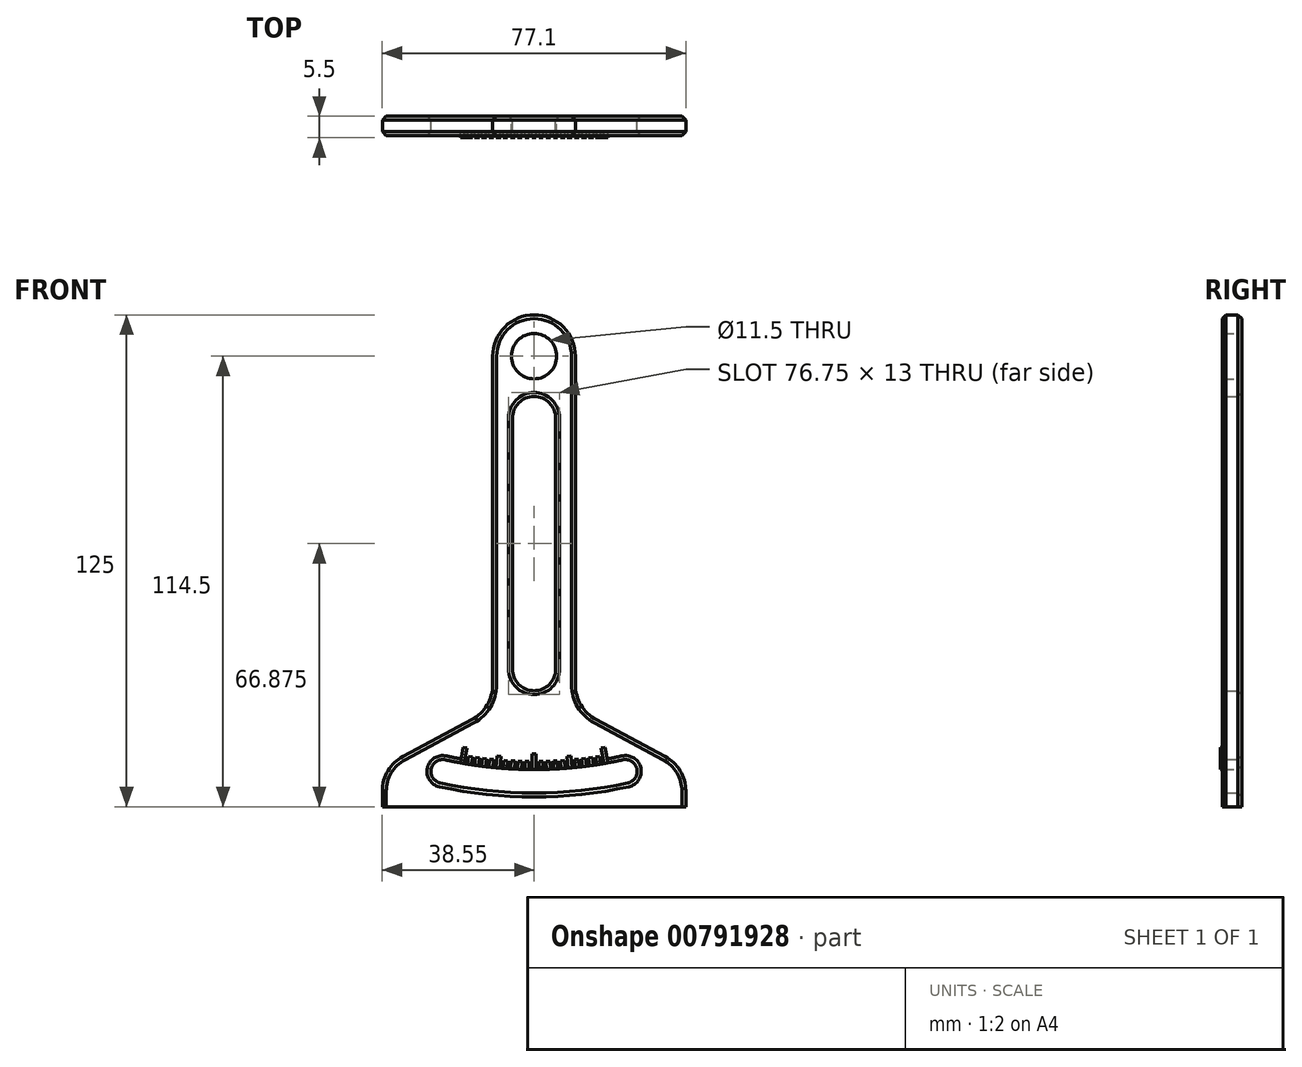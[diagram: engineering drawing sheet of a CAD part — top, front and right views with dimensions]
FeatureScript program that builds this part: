
annotation { "Feature Type Name" : "Feature", "Feature Type Description" : "" }
export const myFeature = defineFeature(function(context is Context, id is Id, definition is map)
    precondition{}
    {
        {
            var Q0;
            Q0=qCreatedBy(makeId("Front.planeOp"),FACE);
            var sketch = newSketch(context, id + "F0", { "sketchPlane" : qUnion([Q0])});
            skLineSegment(sketch, "E0", {"start": v(0, 62.5) * mm, "end": v(0, -62.5) * mm, "construction": true});
            skPoint(sketch, "E1", {"position": v(0, 0) * mm});
            skLineSegment(sketch, "E2", {"start": v(0, 62.5) * mm, "end": v(0, 57.5) * mm, "construction": true});
            skLineSegment(sketch, "E3", {"start": v(0, 57.5) * mm, "end": v(0, 52) * mm, "construction": true});
            skCircle(sketch, "E4", {"center": v(0, 52) * mm, "radius": 5.75 * mm});
            skLineSegment(sketch, "E5", {"start": v(-28.55, -62.5) * mm, "end": v(28.55, -62.5) * mm});
            skPoint(sketch, "E6", {"position": v(0, -62.5) * mm});
            skLineSegment(sketch, "E7", {"start": v(0, 52) * mm, "end": v(28.55, -62.5) * mm, "construction": true});
            skLineSegment(sketch, "E8", {"start": v(28.55, -62.5) * mm, "end": v(38.55, -62.5) * mm});
            skLineSegment(sketch, "E9", {"start": v(38.55, -62.5) * mm, "end": v(38.55, -52.5) * mm});
            skLineSegment(sketch, "E10", {"start": v(0, -62.5) * mm, "end": v(0, -37.5) * mm, "construction": true});
            skLineSegment(sketch, "E11", {"start": v(-10.5, -37.5) * mm, "end": v(10.5, -37.5) * mm, "construction": true});
            skPoint(sketch, "E12", {"position": v(0, -37.5) * mm});
            skLineSegment(sketch, "E13", {"start": v(38.55, -52.5) * mm, "end": v(10.5, -37.5) * mm});
            skLineSegment(sketch, "E14", {"start": v(10.5, -37.5) * mm, "end": v(10.5, 52) * mm});
            skLineSegment(sketch, "E15", {"start": v(28.55, -62.5) * mm, "end": v(26.13, -52.8) * mm, "construction": true});
            skLineSegment(sketch, "E16.MirrorCS", {"start": v(-38.55, -52.5) * mm, "end": v(-10.5, -37.5) * mm});
            skLineSegment(sketch, "E17.MirrorCS", {"start": v(-10.5, -37.5) * mm, "end": v(-10.5, 52) * mm});
            skLineSegment(sketch, "E18.MirrorCS", {"start": v(-38.55, -62.5) * mm, "end": v(-38.55, -52.5) * mm});
            skLineSegment(sketch, "E19.MirrorCS", {"start": v(-28.55, -62.5) * mm, "end": v(-38.55, -62.5) * mm});
            skLineSegment(sketch, "E20.MirrorCS", {"start": v(0, 52) * mm, "end": v(-28.55, -62.5) * mm, "construction": true});
            skLineSegment(sketch, "E21.MirrorCS", {"start": v(-28.55, -62.5) * mm, "end": v(-26.13, -52.8) * mm, "construction": true});
            skArc(sketch, "E22", {"start": v(-26.13, -52.8) * mm, "mid": v(0, -56) * mm, "end": v(26.13, -52.8) * mm, "construction": true});
            skArc(sketch, "E23.0", {"start": v(-25.4, -49.89) * mm, "mid": v(0, -53) * mm, "end": v(25.4, -49.89) * mm});
            skArc(sketch, "E24.0", {"start": v(-26.85, -55.7) * mm, "mid": v(0, -59) * mm, "end": v(26.85, -55.7) * mm});
            skLineSegment(sketch, "E25", {"start": v(-26.85, -55.7) * mm, "end": v(-25.4, -49.89) * mm});
            skLineSegment(sketch, "E26", {"start": v(26.85, -55.7) * mm, "end": v(25.4, -49.89) * mm});
            skArc(sketch, "E27", {"start": v(10.5, 52) * mm, "mid": v(0, 62.5) * mm, "end": v(-10.5, 52) * mm});
            skLineSegment(sketch, "E28", {"start": v(0, 46.25) * mm, "end": v(0, 36.25) * mm, "construction": true});
            skLineSegment(sketch, "E29", {"start": v(0, -37.5) * mm, "end": v(0, -27.5) * mm, "construction": true});
            skArc(sketch, "E30", {"start": v(-5.5, -27.5) * mm, "mid": v(0, -33) * mm, "end": v(5.5, -27.5) * mm});
            skArc(sketch, "E31", {"start": v(5.5, 36.25) * mm, "mid": v(0, 41.75) * mm, "end": v(-5.5, 36.25) * mm});
            skLineSegment(sketch, "E32", {"start": v(-5.5, 36.25) * mm, "end": v(-5.5, -27.5) * mm});
            skLineSegment(sketch, "E33", {"start": v(5.5, 36.25) * mm, "end": v(5.5, -27.5) * mm});
            skSolve(sketch);
        }
        {
            var Q0;
            Q0=makeQuery(id+"F0.imprint","IMPRINT",FACE,{"disambiguationData":[TD([[makeQuery(id+"F0.imprint","IMPRINT",EDGE,{"derivedFrom":sQuery(id+"F0.wireOp",EDGE,"E4")}),-1.0]])]});
            extrude(context, id + "F1", {"entities" : qUnion([Q0]), "depth" : 5 * mm, "offsetDistance" : 25 * mm});
        }
        {
            var Q0;
            Q0=makeQuery(id+"F1.opExtrude","CAP_FACE",FACE,{"disambiguationData":[OSD([sQuery(id+"F0.wireOp",EDGE,"E4"),sQuery(id+"F0.wireOp",EDGE,"E5"),sQuery(id+"F0.wireOp",EDGE,"E8"),sQuery(id+"F0.wireOp",EDGE,"E9"),sQuery(id+"F0.wireOp",EDGE,"E13"),sQuery(id+"F0.wireOp",EDGE,"E14"),sQuery(id+"F0.wireOp",EDGE,"E16.MirrorCS"),sQuery(id+"F0.wireOp",EDGE,"E17.MirrorCS"),sQuery(id+"F0.wireOp",EDGE,"E18.MirrorCS"),sQuery(id+"F0.wireOp",EDGE,"E19.MirrorCS"),sQuery(id+"F0.wireOp",EDGE,"E23.0"),sQuery(id+"F0.wireOp",EDGE,"E24.0"),sQuery(id+"F0.wireOp",EDGE,"E25"),sQuery(id+"F0.wireOp",EDGE,"E26"),sQuery(id+"F0.wireOp",EDGE,"E27")])],"isStart":false});
            var sketch = newSketch(context, id + "F2", { "sketchPlane" : qUnion([Q0])});
            skLineSegment(sketch, "E34", {"start": v(1.8, -50.99) * mm, "end": v(2, -62.5) * mm, "construction": true});
            skLineSegment(sketch, "E35", {"start": v(0, 52) * mm, "end": v(0, -62.5) * mm, "construction": true});
            skLineSegment(sketch, "E36", {"start": v(1.83, -52.99) * mm, "end": v(1.8, -50.99) * mm, "construction": true});
            skLineSegment(sketch, "E37", {"start": v(1.3, -51) * mm, "end": v(2.3, -50.98) * mm});
            skPoint(sketch, "E38", {"position": v(1.8, -50.99) * mm});
            skLineSegment(sketch, "E39", {"start": v(1.3, -51) * mm, "end": v(1.33, -53) * mm});
            skLineSegment(sketch, "E40", {"start": v(2.3, -50.98) * mm, "end": v(2.33, -52.99) * mm});
            skLineSegment(sketch, "E41", {"start": v(2.33, -52.99) * mm, "end": v(1.33, -53) * mm});
            skLineSegment(sketch, "E42", {"start": v(0, -53) * mm, "end": v(0, -49) * mm, "construction": true});
            skLineSegment(sketch, "E43", {"start": v(-0.5, -49) * mm, "end": v(0.5, -49) * mm});
            skPoint(sketch, "E44", {"position": v(0, -49) * mm});
            skLineSegment(sketch, "E45", {"start": v(-0.5, -49) * mm, "end": v(-0.5, -53) * mm});
            skLineSegment(sketch, "E46", {"start": v(-0.5, -53) * mm, "end": v(0.5, -53) * mm});
            skLineSegment(sketch, "E47", {"start": v(0.5, -53) * mm, "end": v(0.5, -49) * mm});
            skLineSegment(sketch, "E48", {"start": v(3.6, -50.94) * mm, "end": v(4, -62.5) * mm, "construction": true});
            skLineSegment(sketch, "E49", {"start": v(5.4, -50.86) * mm, "end": v(6, -62.5) * mm, "construction": true});
            skLineSegment(sketch, "E50", {"start": v(7.19, -50.75) * mm, "end": v(8, -62.5) * mm, "construction": true});
            skLineSegment(sketch, "E51", {"start": v(8.9, -49.62) * mm, "end": v(10.02, -62.5) * mm, "construction": true});
            skLineSegment(sketch, "E52", {"start": v(10.77, -50.44) * mm, "end": v(12.03, -62.5) * mm, "construction": true});
            skLineSegment(sketch, "E53", {"start": v(12.55, -50.24) * mm, "end": v(14.06, -62.5) * mm, "construction": true});
            skLineSegment(sketch, "E54", {"start": v(14.34, -50) * mm, "end": v(16.1, -62.5) * mm, "construction": true});
            skLineSegment(sketch, "E55", {"start": v(16.11, -49.74) * mm, "end": v(18.14, -62.5) * mm, "construction": true});
            skLineSegment(sketch, "E56", {"start": v(17.54, -47.47) * mm, "end": v(20.19, -62.5) * mm, "construction": true});
            skLineSegment(sketch, "E57", {"start": v(3.66, -52.94) * mm, "end": v(3.6, -50.94) * mm, "construction": true});
            skLineSegment(sketch, "E58", {"start": v(5.5, -52.86) * mm, "end": v(5.4, -50.86) * mm, "construction": true});
            skLineSegment(sketch, "E59", {"start": v(7.32, -52.75) * mm, "end": v(7.19, -50.75) * mm, "construction": true});
            skLineSegment(sketch, "E60", {"start": v(9.15, -52.6) * mm, "end": v(8.9, -49.62) * mm, "construction": true});
            skLineSegment(sketch, "E61", {"start": v(10.98, -52.43) * mm, "end": v(10.77, -50.44) * mm, "construction": true});
            skLineSegment(sketch, "E62", {"start": v(12.8, -52.22) * mm, "end": v(12.55, -50.24) * mm, "construction": true});
            skLineSegment(sketch, "E63", {"start": v(14.61, -51.98) * mm, "end": v(14.34, -50) * mm, "construction": true});
            skLineSegment(sketch, "E64", {"start": v(16.43, -51.71) * mm, "end": v(16.11, -49.74) * mm, "construction": true});
            skLineSegment(sketch, "E65", {"start": v(18.23, -51.4) * mm, "end": v(17.54, -47.47) * mm, "construction": true});
            skLineSegment(sketch, "E66", {"start": v(17.05, -47.56) * mm, "end": v(18.03, -47.38) * mm});
            skPoint(sketch, "E67", {"position": v(17.54, -47.47) * mm});
            skLineSegment(sketch, "E68", {"start": v(17.05, -47.56) * mm, "end": v(17.74, -51.5) * mm});
            skLineSegment(sketch, "E69", {"start": v(18.03, -47.38) * mm, "end": v(18.73, -51.32) * mm});
            skLineSegment(sketch, "E70", {"start": v(15.62, -49.82) * mm, "end": v(16.6, -49.66) * mm});
            skPoint(sketch, "E71", {"position": v(16.11, -49.74) * mm});
            skLineSegment(sketch, "E72", {"start": v(15.62, -49.82) * mm, "end": v(15.93, -51.79) * mm});
            skLineSegment(sketch, "E73", {"start": v(16.6, -49.66) * mm, "end": v(16.92, -51.63) * mm});
            skLineSegment(sketch, "E74", {"start": v(13.84, -50.07) * mm, "end": v(14.83, -49.93) * mm});
            skPoint(sketch, "E75", {"position": v(14.34, -50) * mm});
            skLineSegment(sketch, "E76", {"start": v(13.84, -50.07) * mm, "end": v(14.12, -52.05) * mm});
            skLineSegment(sketch, "E77", {"start": v(14.83, -49.93) * mm, "end": v(15.1, -51.91) * mm});
            skLineSegment(sketch, "E78", {"start": v(12.06, -50.3) * mm, "end": v(13.05, -50.18) * mm});
            skPoint(sketch, "E79", {"position": v(12.55, -50.24) * mm});
            skLineSegment(sketch, "E80", {"start": v(12.06, -50.3) * mm, "end": v(12.3, -52.28) * mm});
            skLineSegment(sketch, "E81", {"start": v(13.05, -50.18) * mm, "end": v(13.3, -52.16) * mm});
            skLineSegment(sketch, "E82", {"start": v(10.27, -50.5) * mm, "end": v(11.26, -50.39) * mm});
            skPoint(sketch, "E83.positionSnap0", {"position": v(10.77, -50.44) * mm});
            skLineSegment(sketch, "E84", {"start": v(10.27, -50.5) * mm, "end": v(10.48, -52.48) * mm});
            skLineSegment(sketch, "E85", {"start": v(11.26, -50.39) * mm, "end": v(11.47, -52.38) * mm});
            skLineSegment(sketch, "E86", {"start": v(8.4, -49.66) * mm, "end": v(9.39, -49.57) * mm});
            skPoint(sketch, "E87", {"position": v(8.9, -49.62) * mm});
            skLineSegment(sketch, "E88", {"start": v(8.4, -49.66) * mm, "end": v(8.65, -52.65) * mm});
            skLineSegment(sketch, "E89", {"start": v(9.39, -49.57) * mm, "end": v(9.65, -52.56) * mm});
            skLineSegment(sketch, "E90", {"start": v(6.69, -50.79) * mm, "end": v(7.68, -50.72) * mm});
            skPoint(sketch, "E91", {"position": v(7.19, -50.75) * mm});
            skLineSegment(sketch, "E92", {"start": v(6.69, -50.79) * mm, "end": v(6.83, -52.78) * mm});
            skLineSegment(sketch, "E93", {"start": v(7.68, -50.72) * mm, "end": v(7.82, -52.71) * mm});
            skLineSegment(sketch, "E94", {"start": v(4.9, -50.9) * mm, "end": v(5.9, -50.84) * mm});
            skPoint(sketch, "E95.positionSnap0", {"position": v(5.4, -50.86) * mm});
            skLineSegment(sketch, "E96", {"start": v(4.9, -50.9) * mm, "end": v(5, -52.89) * mm});
            skLineSegment(sketch, "E97", {"start": v(5.9, -50.84) * mm, "end": v(6, -52.83) * mm});
            skLineSegment(sketch, "E98", {"start": v(3.1, -50.96) * mm, "end": v(4.1, -50.93) * mm});
            skPoint(sketch, "E99", {"position": v(3.6, -50.94) * mm});
            skLineSegment(sketch, "E100", {"start": v(3.1, -50.96) * mm, "end": v(3.16, -52.96) * mm});
            skLineSegment(sketch, "E101", {"start": v(4.1, -50.93) * mm, "end": v(4.16, -52.92) * mm});
            skLineSegment(sketch, "E102.MirrorCS", {"start": v(-1.3, -51) * mm, "end": v(-1.33, -53) * mm});
            skLineSegment(sketch, "E103.MirrorCS", {"start": v(-1.3, -51) * mm, "end": v(-2.3, -50.98) * mm});
            skLineSegment(sketch, "E104.MirrorCS", {"start": v(-2.3, -50.98) * mm, "end": v(-2.33, -52.99) * mm});
            skLineSegment(sketch, "E105.MirrorCS", {"start": v(-3.1, -50.96) * mm, "end": v(-3.16, -52.96) * mm});
            skLineSegment(sketch, "E106.MirrorCS", {"start": v(-3.1, -50.96) * mm, "end": v(-4.1, -50.93) * mm});
            skLineSegment(sketch, "E107.MirrorCS", {"start": v(-4.1, -50.93) * mm, "end": v(-4.16, -52.92) * mm});
            skLineSegment(sketch, "E108.MirrorCS", {"start": v(-4.9, -50.9) * mm, "end": v(-5, -52.89) * mm});
            skLineSegment(sketch, "E109.MirrorCS", {"start": v(-4.9, -50.9) * mm, "end": v(-5.9, -50.84) * mm});
            skLineSegment(sketch, "E110.MirrorCS", {"start": v(-5.9, -50.84) * mm, "end": v(-6, -52.83) * mm});
            skLineSegment(sketch, "E111.MirrorCS", {"start": v(-6.69, -50.79) * mm, "end": v(-6.83, -52.78) * mm});
            skLineSegment(sketch, "E112.MirrorCS", {"start": v(-6.69, -50.79) * mm, "end": v(-7.68, -50.72) * mm});
            skLineSegment(sketch, "E113.MirrorCS", {"start": v(-7.68, -50.72) * mm, "end": v(-7.82, -52.71) * mm});
            skLineSegment(sketch, "E114.MirrorCS", {"start": v(-8.4, -49.66) * mm, "end": v(-8.65, -52.65) * mm});
            skLineSegment(sketch, "E115.MirrorCS", {"start": v(-8.4, -49.66) * mm, "end": v(-9.39, -49.57) * mm});
            skLineSegment(sketch, "E116.MirrorCS", {"start": v(-9.39, -49.57) * mm, "end": v(-9.65, -52.56) * mm});
            skLineSegment(sketch, "E117.MirrorCS", {"start": v(-10.27, -50.5) * mm, "end": v(-10.48, -52.48) * mm});
            skLineSegment(sketch, "E118.MirrorCS", {"start": v(-10.27, -50.5) * mm, "end": v(-11.26, -50.39) * mm});
            skLineSegment(sketch, "E119.MirrorCS", {"start": v(-11.26, -50.39) * mm, "end": v(-11.47, -52.38) * mm});
            skLineSegment(sketch, "E120.MirrorCS", {"start": v(-12.06, -50.3) * mm, "end": v(-12.3, -52.28) * mm});
            skLineSegment(sketch, "E121.MirrorCS", {"start": v(-12.06, -50.3) * mm, "end": v(-13.05, -50.18) * mm});
            skLineSegment(sketch, "E122.MirrorCS", {"start": v(-13.05, -50.18) * mm, "end": v(-13.3, -52.16) * mm});
            skLineSegment(sketch, "E123.MirrorCS", {"start": v(-13.84, -50.07) * mm, "end": v(-14.12, -52.05) * mm});
            skLineSegment(sketch, "E124.MirrorCS", {"start": v(-13.84, -50.07) * mm, "end": v(-14.83, -49.93) * mm});
            skLineSegment(sketch, "E125.MirrorCS", {"start": v(-14.83, -49.93) * mm, "end": v(-15.1, -51.91) * mm});
            skLineSegment(sketch, "E126.MirrorCS", {"start": v(-15.62, -49.82) * mm, "end": v(-15.93, -51.79) * mm});
            skLineSegment(sketch, "E127.MirrorCS", {"start": v(-15.62, -49.82) * mm, "end": v(-16.6, -49.66) * mm});
            skLineSegment(sketch, "E128.MirrorCS", {"start": v(-16.6, -49.66) * mm, "end": v(-16.92, -51.63) * mm});
            skLineSegment(sketch, "E129.MirrorCS", {"start": v(-17.05, -47.56) * mm, "end": v(-17.74, -51.5) * mm});
            skLineSegment(sketch, "E130.MirrorCS", {"start": v(-17.05, -47.56) * mm, "end": v(-18.03, -47.38) * mm});
            skLineSegment(sketch, "E131.MirrorCS", {"start": v(-18.03, -47.38) * mm, "end": v(-18.73, -51.32) * mm});
            skSolve(sketch);
        }
        {
            var Q0;
            {var subQ0=sQuery(id+"F2.wireOp",EDGE,"E37");Q0=makeQuery(id+"F2.imprint","IMPRINT",FACE,{"disambiguationData":[TD([[makeQuery(id+"F2.imprint","IMPRINT",EDGE,{"derivedFrom":subQ0}),-1.0]])]});}
            var Q1;
            Q1=makeQuery(id+"F2.imprint","IMPRINT",FACE,{"disambiguationData":[TD([[makeQuery(id+"F2.imprint","IMPRINT",EDGE,{"derivedFrom":sQuery(id+"F2.wireOp",EDGE,"E74")}),-1.0]])]});
            var Q2;
            Q2=makeQuery(id+"F2.imprint","IMPRINT",FACE,{"disambiguationData":[TD([[makeQuery(id+"F2.imprint","IMPRINT",EDGE,{"derivedFrom":sQuery(id+"F2.wireOp",EDGE,"E70")}),-1.0]])]});
            var Q3;
            Q3=makeQuery(id+"F2.imprint","IMPRINT",FACE,{"disambiguationData":[TD([[makeQuery(id+"F2.imprint","IMPRINT",EDGE,{"derivedFrom":sQuery(id+"F2.wireOp",EDGE,"E66")}),-1.0]])]});
            var Q4;
            {var subQ0=sQuery(id+"F2.wireOp",EDGE,"E43");Q4=makeQuery(id+"F2.imprint","IMPRINT",FACE,{"disambiguationData":[TD([[makeQuery(id+"F2.imprint","IMPRINT",EDGE,{"derivedFrom":subQ0}),-1.0]])]});}
            var Q5;
            Q5=makeQuery(id+"F2.imprint","IMPRINT",FACE,{"disambiguationData":[TD([[makeQuery(id+"F2.imprint","IMPRINT",EDGE,{"derivedFrom":sQuery(id+"F2.wireOp",EDGE,"E98")}),-1.0]])]});
            var Q6;
            Q6=makeQuery(id+"F2.imprint","IMPRINT",FACE,{"disambiguationData":[TD([[makeQuery(id+"F2.imprint","IMPRINT",EDGE,{"derivedFrom":sQuery(id+"F2.wireOp",EDGE,"E94")}),-1.0]])]});
            var Q7;
            Q7=makeQuery(id+"F2.imprint","IMPRINT",FACE,{"disambiguationData":[TD([[makeQuery(id+"F2.imprint","IMPRINT",EDGE,{"derivedFrom":sQuery(id+"F2.wireOp",EDGE,"E90")}),-1.0]])]});
            var Q8;
            Q8=makeQuery(id+"F2.imprint","IMPRINT",FACE,{"disambiguationData":[TD([[makeQuery(id+"F2.imprint","IMPRINT",EDGE,{"derivedFrom":sQuery(id+"F2.wireOp",EDGE,"E86")}),-1.0]])]});
            var Q9;
            Q9=makeQuery(id+"F2.imprint","IMPRINT",FACE,{"disambiguationData":[TD([[makeQuery(id+"F2.imprint","IMPRINT",EDGE,{"derivedFrom":sQuery(id+"F2.wireOp",EDGE,"E82")}),-1.0]])]});
            var Q10;
            Q10=makeQuery(id+"F2.imprint","IMPRINT",FACE,{"disambiguationData":[TD([[makeQuery(id+"F2.imprint","IMPRINT",EDGE,{"derivedFrom":sQuery(id+"F2.wireOp",EDGE,"E78")}),-1.0]])]});
            var Q11;
            {var subQ0=sQuery(id+"F2.wireOp",EDGE,"E102.MirrorCS");Q11=makeQuery(id+"F2.imprint","IMPRINT",FACE,{"disambiguationData":[TD([[makeQuery(id+"F2.imprint","IMPRINT",EDGE,{"derivedFrom":subQ0}),-1.0]])]});}
            var Q12;
            {var subQ0=sQuery(id+"F2.wireOp",EDGE,"E105.MirrorCS");Q12=makeQuery(id+"F2.imprint","IMPRINT",FACE,{"disambiguationData":[TD([[makeQuery(id+"F2.imprint","IMPRINT",EDGE,{"derivedFrom":subQ0}),-1.0]])]});}
            var Q13;
            {var subQ0=sQuery(id+"F2.wireOp",EDGE,"E108.MirrorCS");Q13=makeQuery(id+"F2.imprint","IMPRINT",FACE,{"disambiguationData":[TD([[makeQuery(id+"F2.imprint","IMPRINT",EDGE,{"derivedFrom":subQ0}),-1.0]])]});}
            var Q14;
            {var subQ0=sQuery(id+"F2.wireOp",EDGE,"E111.MirrorCS");Q14=makeQuery(id+"F2.imprint","IMPRINT",FACE,{"disambiguationData":[TD([[makeQuery(id+"F2.imprint","IMPRINT",EDGE,{"derivedFrom":subQ0}),-1.0]])]});}
            var Q15;
            {var subQ0=sQuery(id+"F2.wireOp",EDGE,"E114.MirrorCS");Q15=makeQuery(id+"F2.imprint","IMPRINT",FACE,{"disambiguationData":[TD([[makeQuery(id+"F2.imprint","IMPRINT",EDGE,{"derivedFrom":subQ0}),-1.0]])]});}
            var Q16;
            {var subQ0=sQuery(id+"F2.wireOp",EDGE,"E117.MirrorCS");Q16=makeQuery(id+"F2.imprint","IMPRINT",FACE,{"disambiguationData":[TD([[makeQuery(id+"F2.imprint","IMPRINT",EDGE,{"derivedFrom":subQ0}),-1.0]])]});}
            var Q17;
            {var subQ0=sQuery(id+"F2.wireOp",EDGE,"E120.MirrorCS");Q17=makeQuery(id+"F2.imprint","IMPRINT",FACE,{"disambiguationData":[TD([[makeQuery(id+"F2.imprint","IMPRINT",EDGE,{"derivedFrom":subQ0}),-1.0]])]});}
            var Q18;
            {var subQ0=sQuery(id+"F2.wireOp",EDGE,"E123.MirrorCS");Q18=makeQuery(id+"F2.imprint","IMPRINT",FACE,{"disambiguationData":[TD([[makeQuery(id+"F2.imprint","IMPRINT",EDGE,{"derivedFrom":subQ0}),-1.0]])]});}
            var Q19;
            {var subQ0=sQuery(id+"F2.wireOp",EDGE,"E126.MirrorCS");Q19=makeQuery(id+"F2.imprint","IMPRINT",FACE,{"disambiguationData":[TD([[makeQuery(id+"F2.imprint","IMPRINT",EDGE,{"derivedFrom":subQ0}),-1.0]])]});}
            var Q20;
            {var subQ0=sQuery(id+"F2.wireOp",EDGE,"E129.MirrorCS");Q20=makeQuery(id+"F2.imprint","IMPRINT",FACE,{"disambiguationData":[TD([[makeQuery(id+"F2.imprint","IMPRINT",EDGE,{"derivedFrom":subQ0}),-1.0]])]});}
            extrude(context, id + "F3", {"entities" : qUnion([Q0, Q1, Q2, Q3, Q4, Q5, Q6, Q7, Q8, Q9, Q10, Q11, Q12, Q13, Q14, Q15, Q16, Q17, Q18, Q19, Q20]), "operationType" : NewBodyOperationType.ADD, "depth" : .5 * mm, "offsetDistance" : 25 * mm});
        }
        {
            var Q0;
            Q0=makeQuery(id+"F1.opExtrude","SWEPT_EDGE",EDGE,{"disambiguationData":[OSD([sQuery(id+"F0.wireOp",EDGE,"E13"),sQuery(id+"F0.wireOp",EDGE,"E14")])]});
            var Q1;
            Q1=makeQuery(id+"F1.opExtrude","SWEPT_EDGE",EDGE,{"disambiguationData":[OSD([sQuery(id+"F0.wireOp",EDGE,"E16.MirrorCS"),sQuery(id+"F0.wireOp",EDGE,"E17.MirrorCS")])]});
            var Q2;
            Q2=makeQuery(id+"F1.opExtrude","SWEPT_EDGE",EDGE,{"disambiguationData":[OSD([sQuery(id+"F0.wireOp",EDGE,"E16.MirrorCS"),sQuery(id+"F0.wireOp",EDGE,"E18.MirrorCS")])]});
            var Q3;
            Q3=makeQuery(id+"F1.opExtrude","SWEPT_EDGE",EDGE,{"disambiguationData":[OSD([sQuery(id+"F0.wireOp",EDGE,"E9"),sQuery(id+"F0.wireOp",EDGE,"E13")])]});
            fillet(context, id + "F4", {"entities" : qUnion([Q0, Q1, Q2, Q3]), "radius" : 10 * mm, "tangentPropagation" : true, "allowEdgeOverflow" : false});
        }
        {
            var Q0;
            Q0=makeQuery(id+"F1.opExtrude","SWEPT_EDGE",EDGE,{"disambiguationData":[OSD([sQuery(id+"F0.wireOp",EDGE,"E23.0"),sQuery(id+"F0.wireOp",EDGE,"E25")])]});
            var Q1;
            Q1=makeQuery(id+"F1.opExtrude","SWEPT_EDGE",EDGE,{"disambiguationData":[OSD([sQuery(id+"F0.wireOp",EDGE,"E24.0"),sQuery(id+"F0.wireOp",EDGE,"E25")])]});
            var Q2;
            Q2=makeQuery(id+"F1.opExtrude","SWEPT_EDGE",EDGE,{"disambiguationData":[OSD([sQuery(id+"F0.wireOp",EDGE,"E23.0"),sQuery(id+"F0.wireOp",EDGE,"E26")])]});
            var Q3;
            Q3=makeQuery(id+"F1.opExtrude","SWEPT_EDGE",EDGE,{"disambiguationData":[OSD([sQuery(id+"F0.wireOp",EDGE,"E24.0"),sQuery(id+"F0.wireOp",EDGE,"E26")])]});
            fillet(context, id + "F5", {"entities" : qUnion([Q0, Q1, Q2, Q3]), "radius" : 3 * mm, "tangentPropagation" : true, "allowEdgeOverflow" : false});
        }
        {
            var Q0;
            Q0=makeQuery(id+"F1.opExtrude","CAP_EDGE",EDGE,{"disambiguationData":[OSD([sQuery(id+"F0.wireOp",EDGE,"E13")])],"isStart":false});
            var Q1;
            Q1=makeQuery(id+"F1.opExtrude","CAP_EDGE",EDGE,{"disambiguationData":[OSD([sQuery(id+"F0.wireOp",EDGE,"E13")])],"isStart":true});
            var Q2;
            Q2=makeQuery(id+"F1.opExtrude","CAP_EDGE",EDGE,{"disambiguationData":[OSD([sQuery(id+"F0.wireOp",EDGE,"E30")])],"isStart":false});
            var Q3;
            Q3=makeQuery(id+"F1.opExtrude","CAP_EDGE",EDGE,{"disambiguationData":[OSD([sQuery(id+"F0.wireOp",EDGE,"E30")])],"isStart":true});
            var Q4;
            Q4=makeQuery(id+"F1.opExtrude","CAP_EDGE",EDGE,{"disambiguationData":[OSD([sQuery(id+"F0.wireOp",EDGE,"E24.0")])],"isStart":false});
            var Q5;
            Q5=makeQuery(id+"F1.opExtrude","CAP_EDGE",EDGE,{"disambiguationData":[OSD([sQuery(id+"F0.wireOp",EDGE,"E23.0")])],"isStart":true});
            var Q6;
            {var subQ0=sQuery(id+"F0.wireOp",EDGE,"E23.0");var subQ1=makeQuery(id+"F1.opExtrude","CAP_EDGE",EDGE,{"disambiguationData":[OSD([subQ0])],"isStart":false});var subQ3=sQuery(id+"F2.wireOp",EDGE,"E128.MirrorCS");Q6=makeQuery(id+"F3.boolean.opBoolean","SPLIT",EDGE,{"disambiguationData":[TD([makeQuery(id+"F3.opExtrude","SWEPT_FACE",FACE,{"disambiguationData":[OSD([subQ3])]})])],"derivedFrom":subQ1});}
            var Q7;
            {var subQ0=sQuery(id+"F0.wireOp",EDGE,"E23.0");var subQ1=makeQuery(id+"F1.opExtrude","CAP_EDGE",EDGE,{"disambiguationData":[OSD([subQ0])],"isStart":false});var subQ2=sQuery(id+"F2.wireOp",EDGE,"E125.MirrorCS");Q7=makeQuery(id+"F3.boolean.opBoolean","SPLIT",EDGE,{"disambiguationData":[TD([makeQuery(id+"F3.opExtrude","SWEPT_FACE",FACE,{"disambiguationData":[OSD([subQ2])]})])],"derivedFrom":subQ1});}
            var Q8;
            {var subQ0=sQuery(id+"F0.wireOp",EDGE,"E23.0");var subQ1=makeQuery(id+"F1.opExtrude","CAP_EDGE",EDGE,{"disambiguationData":[OSD([subQ0])],"isStart":false});var subQ3=sQuery(id+"F2.wireOp",EDGE,"E122.MirrorCS");Q8=makeQuery(id+"F3.boolean.opBoolean","SPLIT",EDGE,{"disambiguationData":[TD([makeQuery(id+"F3.opExtrude","SWEPT_FACE",FACE,{"disambiguationData":[OSD([subQ3])]})])],"derivedFrom":subQ1});}
            var Q9;
            {var subQ0=sQuery(id+"F0.wireOp",EDGE,"E23.0");var subQ1=makeQuery(id+"F1.opExtrude","CAP_EDGE",EDGE,{"disambiguationData":[OSD([subQ0])],"isStart":false});var subQ3=sQuery(id+"F2.wireOp",EDGE,"E119.MirrorCS");Q9=makeQuery(id+"F3.boolean.opBoolean","SPLIT",EDGE,{"disambiguationData":[TD([makeQuery(id+"F3.opExtrude","SWEPT_FACE",FACE,{"disambiguationData":[OSD([subQ3])]})])],"derivedFrom":subQ1});}
            var Q10;
            {var subQ0=sQuery(id+"F0.wireOp",EDGE,"E23.0");var subQ1=makeQuery(id+"F1.opExtrude","CAP_EDGE",EDGE,{"disambiguationData":[OSD([subQ0])],"isStart":false});var subQ3=sQuery(id+"F2.wireOp",EDGE,"E116.MirrorCS");Q10=makeQuery(id+"F3.boolean.opBoolean","SPLIT",EDGE,{"disambiguationData":[TD([makeQuery(id+"F3.opExtrude","SWEPT_FACE",FACE,{"disambiguationData":[OSD([subQ3])]})])],"derivedFrom":subQ1});}
            var Q11;
            {var subQ0=sQuery(id+"F0.wireOp",EDGE,"E23.0");var subQ1=makeQuery(id+"F1.opExtrude","CAP_EDGE",EDGE,{"disambiguationData":[OSD([subQ0])],"isStart":false});var subQ3=sQuery(id+"F2.wireOp",EDGE,"E113.MirrorCS");Q11=makeQuery(id+"F3.boolean.opBoolean","SPLIT",EDGE,{"disambiguationData":[TD([makeQuery(id+"F3.opExtrude","SWEPT_FACE",FACE,{"disambiguationData":[OSD([subQ3])]})])],"derivedFrom":subQ1});}
            var Q12;
            {var subQ0=sQuery(id+"F0.wireOp",EDGE,"E23.0");var subQ1=makeQuery(id+"F1.opExtrude","CAP_EDGE",EDGE,{"disambiguationData":[OSD([subQ0])],"isStart":false});var subQ3=sQuery(id+"F2.wireOp",EDGE,"E110.MirrorCS");Q12=makeQuery(id+"F3.boolean.opBoolean","SPLIT",EDGE,{"disambiguationData":[TD([makeQuery(id+"F3.opExtrude","SWEPT_FACE",FACE,{"disambiguationData":[OSD([subQ3])]})])],"derivedFrom":subQ1});}
            var Q13;
            {var subQ0=sQuery(id+"F0.wireOp",EDGE,"E23.0");var subQ1=makeQuery(id+"F1.opExtrude","CAP_EDGE",EDGE,{"disambiguationData":[OSD([subQ0])],"isStart":false});var subQ3=sQuery(id+"F2.wireOp",EDGE,"E107.MirrorCS");Q13=makeQuery(id+"F3.boolean.opBoolean","SPLIT",EDGE,{"disambiguationData":[TD([makeQuery(id+"F3.opExtrude","SWEPT_FACE",FACE,{"disambiguationData":[OSD([subQ3])]})])],"derivedFrom":subQ1});}
            var Q14;
            {var subQ0=sQuery(id+"F0.wireOp",EDGE,"E23.0");var subQ1=makeQuery(id+"F1.opExtrude","CAP_EDGE",EDGE,{"disambiguationData":[OSD([subQ0])],"isStart":false});var subQ3=sQuery(id+"F2.wireOp",EDGE,"E104.MirrorCS");Q14=makeQuery(id+"F3.boolean.opBoolean","SPLIT",EDGE,{"disambiguationData":[TD([makeQuery(id+"F3.opExtrude","SWEPT_FACE",FACE,{"disambiguationData":[OSD([subQ3])]})])],"derivedFrom":subQ1});}
            var Q15;
            {var subQ0=sQuery(id+"F0.wireOp",EDGE,"E23.0");var subQ1=makeQuery(id+"F1.opExtrude","CAP_EDGE",EDGE,{"disambiguationData":[OSD([subQ0])],"isStart":false});var subQ3=sQuery(id+"F2.wireOp",EDGE,"E45");Q15=makeQuery(id+"F3.boolean.opBoolean","SPLIT",EDGE,{"disambiguationData":[TD([makeQuery(id+"F3.opExtrude","SWEPT_FACE",FACE,{"disambiguationData":[OSD([subQ3])]})])],"derivedFrom":subQ1});}
            var Q16;
            {var subQ0=sQuery(id+"F0.wireOp",EDGE,"E23.0");var subQ1=makeQuery(id+"F1.opExtrude","CAP_EDGE",EDGE,{"disambiguationData":[OSD([subQ0])],"isStart":false});var subQ2=sQuery(id+"F2.wireOp",EDGE,"E39");Q16=makeQuery(id+"F3.boolean.opBoolean","SPLIT",EDGE,{"disambiguationData":[TD([makeQuery(id+"F3.opExtrude","SWEPT_FACE",FACE,{"disambiguationData":[OSD([subQ2])]})])],"derivedFrom":subQ1});}
            var Q17;
            {var subQ0=sQuery(id+"F0.wireOp",EDGE,"E23.0");var subQ1=makeQuery(id+"F1.opExtrude","CAP_EDGE",EDGE,{"disambiguationData":[OSD([subQ0])],"isStart":false});var subQ3=sQuery(id+"F2.wireOp",EDGE,"E40");Q17=makeQuery(id+"F3.boolean.opBoolean","SPLIT",EDGE,{"disambiguationData":[TD([makeQuery(id+"F3.opExtrude","SWEPT_FACE",FACE,{"disambiguationData":[OSD([subQ3])]})])],"derivedFrom":subQ1});}
            var Q18;
            {var subQ0=sQuery(id+"F0.wireOp",EDGE,"E23.0");var subQ1=makeQuery(id+"F1.opExtrude","CAP_EDGE",EDGE,{"disambiguationData":[OSD([subQ0])],"isStart":false});var subQ2=sQuery(id+"F2.wireOp",EDGE,"E96");Q18=makeQuery(id+"F3.boolean.opBoolean","SPLIT",EDGE,{"disambiguationData":[TD([makeQuery(id+"F3.opExtrude","SWEPT_FACE",FACE,{"disambiguationData":[OSD([subQ2])]})])],"derivedFrom":subQ1});}
            var Q19;
            {var subQ0=sQuery(id+"F0.wireOp",EDGE,"E23.0");var subQ1=makeQuery(id+"F1.opExtrude","CAP_EDGE",EDGE,{"disambiguationData":[OSD([subQ0])],"isStart":false});var subQ2=sQuery(id+"F2.wireOp",EDGE,"E92");Q19=makeQuery(id+"F3.boolean.opBoolean","SPLIT",EDGE,{"disambiguationData":[TD([makeQuery(id+"F3.opExtrude","SWEPT_FACE",FACE,{"disambiguationData":[OSD([subQ2])]})])],"derivedFrom":subQ1});}
            var Q20;
            {var subQ0=sQuery(id+"F0.wireOp",EDGE,"E23.0");var subQ1=makeQuery(id+"F1.opExtrude","CAP_EDGE",EDGE,{"disambiguationData":[OSD([subQ0])],"isStart":false});var subQ3=sQuery(id+"F2.wireOp",EDGE,"E88");Q20=makeQuery(id+"F3.boolean.opBoolean","SPLIT",EDGE,{"disambiguationData":[TD([makeQuery(id+"F3.opExtrude","SWEPT_FACE",FACE,{"disambiguationData":[OSD([subQ3])]})])],"derivedFrom":subQ1});}
            var Q21;
            {var subQ0=sQuery(id+"F0.wireOp",EDGE,"E23.0");var subQ1=makeQuery(id+"F1.opExtrude","CAP_EDGE",EDGE,{"disambiguationData":[OSD([subQ0])],"isStart":false});var subQ2=sQuery(id+"F2.wireOp",EDGE,"E84");Q21=makeQuery(id+"F3.boolean.opBoolean","SPLIT",EDGE,{"disambiguationData":[TD([makeQuery(id+"F3.opExtrude","SWEPT_FACE",FACE,{"disambiguationData":[OSD([subQ2])]})])],"derivedFrom":subQ1});}
            var Q22;
            {var subQ0=sQuery(id+"F0.wireOp",EDGE,"E23.0");var subQ1=makeQuery(id+"F1.opExtrude","CAP_EDGE",EDGE,{"disambiguationData":[OSD([subQ0])],"isStart":false});var subQ2=sQuery(id+"F2.wireOp",EDGE,"E80");Q22=makeQuery(id+"F3.boolean.opBoolean","SPLIT",EDGE,{"disambiguationData":[TD([makeQuery(id+"F3.opExtrude","SWEPT_FACE",FACE,{"disambiguationData":[OSD([subQ2])]})])],"derivedFrom":subQ1});}
            var Q23;
            {var subQ0=sQuery(id+"F0.wireOp",EDGE,"E23.0");var subQ1=makeQuery(id+"F1.opExtrude","CAP_EDGE",EDGE,{"disambiguationData":[OSD([subQ0])],"isStart":false});var subQ2=sQuery(id+"F2.wireOp",EDGE,"E76");Q23=makeQuery(id+"F3.boolean.opBoolean","SPLIT",EDGE,{"disambiguationData":[TD([makeQuery(id+"F3.opExtrude","SWEPT_FACE",FACE,{"disambiguationData":[OSD([subQ2])]})])],"derivedFrom":subQ1});}
            var Q24;
            {var subQ0=sQuery(id+"F0.wireOp",EDGE,"E23.0");var subQ1=makeQuery(id+"F1.opExtrude","CAP_EDGE",EDGE,{"disambiguationData":[OSD([subQ0])],"isStart":false});var subQ3=sQuery(id+"F2.wireOp",EDGE,"E72");Q24=makeQuery(id+"F3.boolean.opBoolean","SPLIT",EDGE,{"disambiguationData":[TD([makeQuery(id+"F3.opExtrude","SWEPT_FACE",FACE,{"disambiguationData":[OSD([subQ3])]})])],"derivedFrom":subQ1});}
            var Q25;
            {var subQ0=sQuery(id+"F0.wireOp",EDGE,"E23.0");var subQ1=makeQuery(id+"F1.opExtrude","CAP_EDGE",EDGE,{"disambiguationData":[OSD([subQ0])],"isStart":false});var subQ3=sQuery(id+"F2.wireOp",EDGE,"E68");Q25=makeQuery(id+"F3.boolean.opBoolean","SPLIT",EDGE,{"disambiguationData":[TD([makeQuery(id+"F3.opExtrude","SWEPT_FACE",FACE,{"disambiguationData":[OSD([subQ3])]})])],"derivedFrom":subQ1});}
            chamfer(context, id + "F6", {"entities" : qUnion([Q0, Q1, Q2, Q3, Q4, Q5, Q6, Q7, Q8, Q9, Q10, Q11, Q12, Q13, Q14, Q15, Q16, Q17, Q18, Q19, Q20, Q21, Q22, Q23, Q24, Q25]), "width" : 1 * mm, "tangentPropagation" : true});
        }
    });
